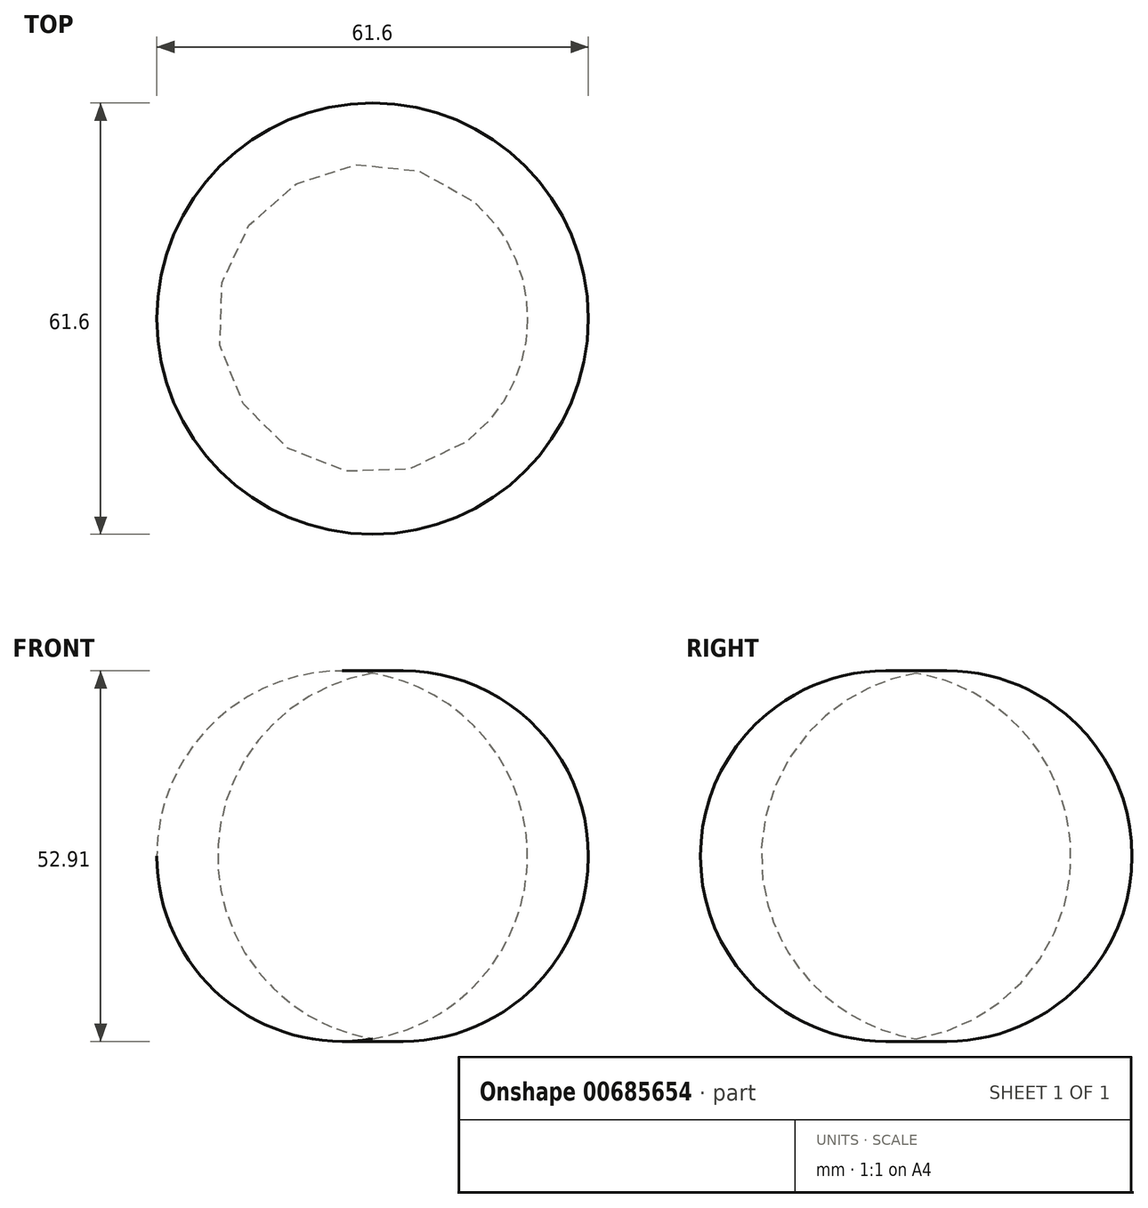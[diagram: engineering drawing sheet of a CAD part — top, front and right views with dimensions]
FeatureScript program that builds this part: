
annotation { "Feature Type Name" : "Feature", "Feature Type Description" : "" }
export const myFeature = defineFeature(function(context is Context, id is Id, definition is map)
    precondition{}
    {
        {
            var Q0;
            Q0=qCreatedBy(makeId("Front.planeOp"),FACE);
            var sketch = newSketch(context, id + "F0", { "sketchPlane" : qUnion([Q0])});
            skLineSegment(sketch, "E0", {"start": v(0, 0) * mm, "end": v(0, 52.2) * mm});
            skArc(sketch, "E1", {"start": v(0, 52.2) * mm, "mid": v(-30.8, 26.1) * mm, "end": v(0, 0) * mm});
            skSolve(sketch);
        }
        {
            var Q0;
            Q0=makeQuery(id+"F0.imprint","IMPRINT",FACE,{"disambiguationData":[TD([[makeQuery(id+"F0.imprint","IMPRINT",EDGE,{"derivedFrom":sQuery(id+"F0.wireOp",EDGE,"E0")}),1.0]])]});
            var Q1;
            Q1=sQuery(id+"F0.wireOp",EDGE,"E0");
            revolve(context, id + "F1", {"entities" : qUnion([Q0]), "axis" : qUnion([Q1]), "revolveType" : RevolveType.FULL});
        }
    });
